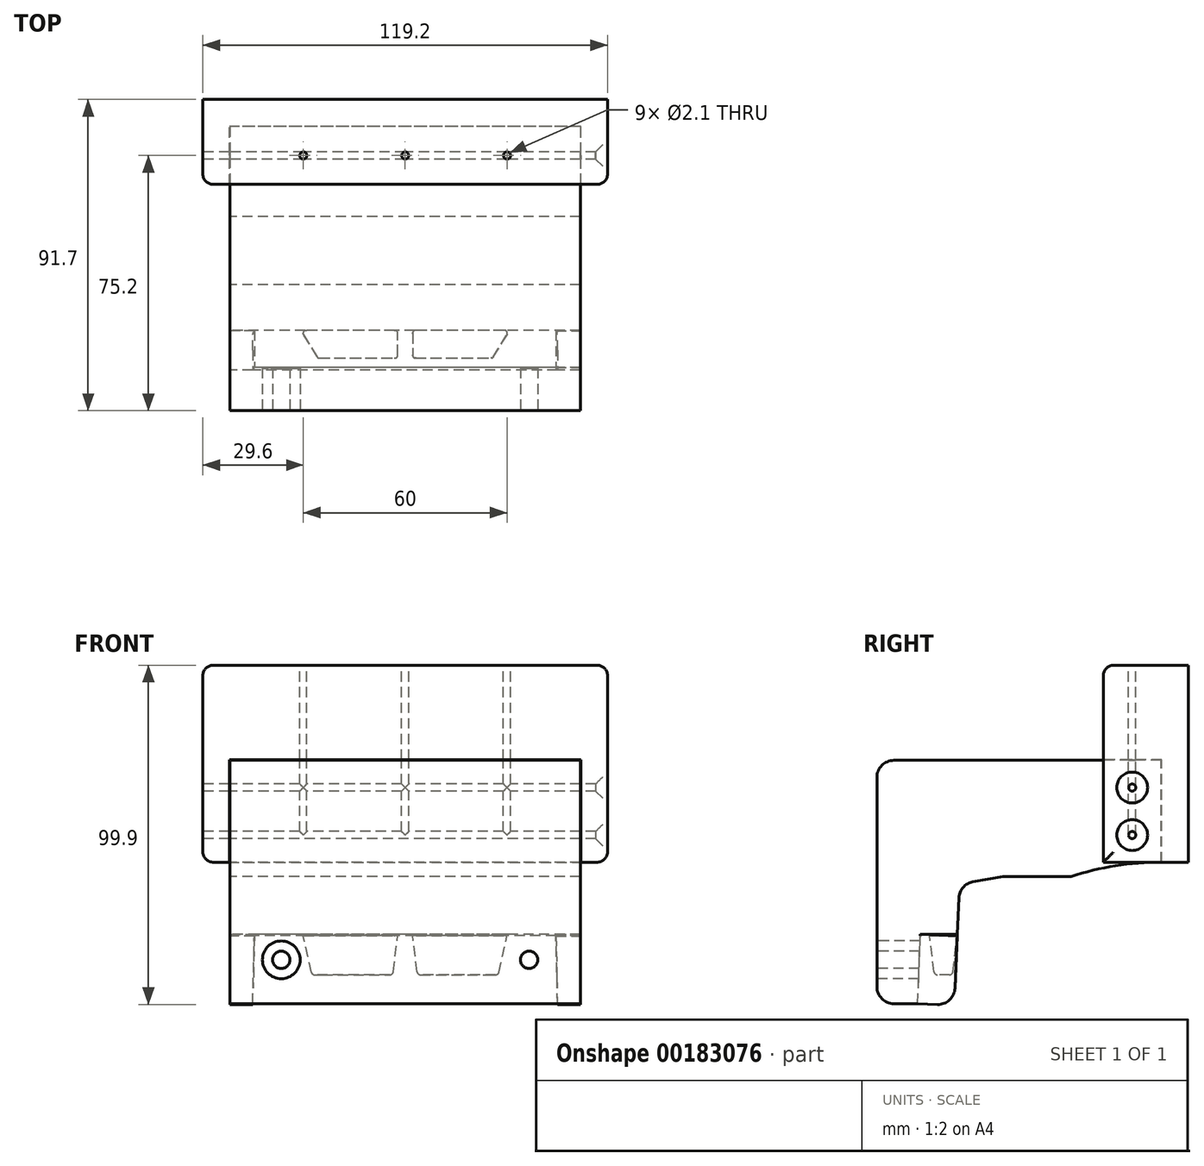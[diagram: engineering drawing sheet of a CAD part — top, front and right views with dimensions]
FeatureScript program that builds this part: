
annotation { "Feature Type Name" : "Feature", "Feature Type Description" : "" }
export const myFeature = defineFeature(function(context is Context, id is Id, definition is map)
    precondition{}
    {
        {
            assignVariable(context, id + "F0", {"name" : "T", "anyValue" : 0.2});
        }
        {
            var Q0;
            Q0=qCreatedBy(makeId("Top.planeOp"),FACE);
            var sketch = newSketch(context, id + "F1", { "sketchPlane" : qUnion([Q0])});
            skLineSegment(sketch, "E0", {"start": v(0, 12.42) * mm, "end": v(0, -41.85) * mm, "construction": true});
            skLineSegment(sketch, "E1.0", {"start": v(2.2, 0) * mm, "end": v(2.2, -8.2) * mm});
            skLineSegment(sketch, "E2", {"start": v(30.8, 0) * mm, "end": v(30.8, 0) * mm});
            skLineSegment(sketch, "E3", {"start": v(2.2, 0) * mm, "end": v(30.8, 0) * mm});
            skLineSegment(sketch, "E4", {"start": v(2.2, -8.2) * mm, "end": v(25.7, -8.2) * mm});
            skLineSegment(sketch, "E5", {"start": v(25.7, -8.2) * mm, "end": v(30.8, 0) * mm});
            skLineSegment(sketch, "E6.MirrorCS", {"start": v(-2.2, 0) * mm, "end": v(-2.2, -8.2) * mm});
            skLineSegment(sketch, "E7.MirrorCS", {"start": v(-2.2, 0) * mm, "end": v(-30.8, 0) * mm});
            skLineSegment(sketch, "E8.MirrorCS", {"start": v(-25.7, -8.2) * mm, "end": v(-30.8, 0) * mm});
            skLineSegment(sketch, "E9.MirrorCS", {"start": v(-2.2, -8.2) * mm, "end": v(-25.7, -8.2) * mm});
            skSolve(sketch);
        }
        {
            var Q0;
            Q0 = qSketchRegion(id + "F1", true);
            extrude(context, id + "F2", {"entities" : qUnion([Q0]), "oppositeDirection" : true, "depth" : 11.5 * mm, "hasDraft" : true, "draftAngle" : 7 * degree, "draftPullDirection" : true});
        }
        {
            var Q0;
            Q0=qCreatedBy(makeId("Right.planeOp"),FACE);
            var sketch = newSketch(context, id + "F3", { "sketchPlane" : qUnion([Q0])});
            skPoint(sketch, "E10.0", {"position": v(-8.2, 0) * mm});
            skLineSegment(sketch, "E11", {"start": v(-10.9, 0) * mm, "end": v(-11.7, -20) * mm});
            skLineSegment(sketch, "E12", {"start": v(-11.7, -20) * mm, "end": v(-23.7, -20) * mm});
            skLineSegment(sketch, "E13", {"start": v(-23.7, -20) * mm, "end": v(-23.7, 0) * mm});
            skLineSegment(sketch, "E14", {"start": v(-10.9, 0) * mm, "end": v(-23.7, 0) * mm});
            skSolve(sketch);
        }
        {
            var Q0;
            Q0=makeQuery(id+"F3.imprint","IMPRINT",FACE,{"disambiguationData":[TD([[makeQuery(id+"F3.imprint","IMPRINT",EDGE,{"derivedFrom":sQuery(id+"F3.wireOp",EDGE,"E11")}),-1.0]])]});
            extrude(context, id + "F4", {"entities" : qUnion([Q0]), "endBound" : BoundingType.SYMMETRIC, "depth" : (103.6 - 2 * getVariable(context, 'T')) * mm});
        }
        {
            var Q0;
            Q0=makeQuery(id+"F4.opExtrude","SWEPT_FACE",FACE,{"disambiguationData":[OSD([sQuery(id+"F3.wireOp",EDGE,"E13")])]});
            var sketch = newSketch(context, id + "F5", { "sketchPlane" : qUnion([Q0])});
            skLineSegment(sketch, "E15", {"start": v(0, 0) * mm, "end": v(0, -20) * mm, "construction": true});
            skLineSegment(sketch, "E16.0", {"start": v(36.5, 0) * mm, "end": v(36.5, -20) * mm, "construction": true});
            skLineSegment(sketch, "E17.0", {"start": v(51.6, -7.1) * mm, "end": v(-51.6, -7.1) * mm, "construction": true});
            skCircle(sketch, "E18", {"center": v(36.5, -7.1) * mm, "radius": 2.55 * mm});
            skCircle(sketch, "E19", {"center": v(36.5, -7.1) * mm, "radius": 5.55 * mm});
            skCircle(sketch, "E20.MirrorC", {"center": v(-36.5, -7.1) * mm, "radius": 2.55 * mm});
            skCircle(sketch, "E21.MirrorC", {"center": v(-36.5, -7.1) * mm, "radius": 5.55 * mm});
            skSolve(sketch);
        }
        {
            var Q0;
            Q0=makeQuery(id+"F5.imprint","IMPRINT",FACE,{"disambiguationData":[TD([[makeQuery(id+"F5.imprint","IMPRINT",EDGE,{"derivedFrom":sQuery(id+"F5.wireOp",EDGE,"E20.MirrorC")}),-1.0]])]});
            var Q1;
            Q1=makeQuery(id+"F5.imprint","IMPRINT",FACE,{"disambiguationData":[TD([[makeQuery(id+"F5.imprint","IMPRINT",EDGE,{"derivedFrom":sQuery(id+"F5.wireOp",EDGE,"E18")}),1.0]])]});
            extrude(context, id + "F6", {"entities" : qUnion([Q0, Q1]), "operationType" : NewBodyOperationType.REMOVE, "endBound" : BoundingType.THROUGH_ALL, "oppositeDirection" : true, "depth" : 25 * mm});
        }
        {
            var Q0;
            Q0=makeQuery(id+"F2.opExtrude","CAP_FACE",FACE,{"disambiguationData":[OSD([sQuery(id+"F1.wireOp",EDGE,"E6.MirrorCS"),sQuery(id+"F1.wireOp",EDGE,"E7.MirrorCS"),sQuery(id+"F1.wireOp",EDGE,"E8.MirrorCS"),sQuery(id+"F1.wireOp",EDGE,"E9.MirrorCS")])],"isStart":true});
            var Q1;
            Q1=makeQuery(id+"F2.opExtrude","CAP_FACE",FACE,{"disambiguationData":[OSD([sQuery(id+"F1.wireOp",EDGE,"E1.0"),sQuery(id+"F1.wireOp",EDGE,"E3"),sQuery(id+"F1.wireOp",EDGE,"E4"),sQuery(id+"F1.wireOp",EDGE,"E5")])],"isStart":true});
            var Q2;
            Q2=makeQuery(id+"F4.opExtrude","SWEPT_FACE",FACE,{"disambiguationData":[OSD([sQuery(id+"F3.wireOp",EDGE,"E14")])]});
            extrude(context, id + "F7", {"entities" : qUnion([Q0, Q1, Q2]), "operationType" : NewBodyOperationType.ADD, "depth" : (2 * getVariable(context, 'T')) * mm});
        }
        {
            var Q0;
            Q0=makeQuery(id+"F4.opExtrude","SWEPT_FACE",FACE,{"disambiguationData":[OSD([sQuery(id+"F3.wireOp",EDGE,"E11")])]});
            var sketch = newSketch(context, id + "F8", { "sketchPlane" : qUnion([Q0])});
            skLineSegment(sketch, "E22", {"start": v(0, -0.44) * mm, "end": v(0, -21.48) * mm, "construction": true});
            skPoint(sketch, "E22.endSnap0", {"position": v(0, -20.45) * mm});
            skLineSegment(sketch, "E23.0", {"start": v(44.4, -0.04) * mm, "end": v(44.4, -20.45) * mm});
            skLineSegment(sketch, "E24", {"start": v(51.6, -0.04) * mm, "end": v(51.6, -20.45) * mm});
            skLineSegment(sketch, "E25", {"start": v(51.6, -20.45) * mm, "end": v(44.4, -20.45) * mm});
            skPoint(sketch, "E26.0", {"position": v(51.6, -20.45) * mm});
            skLineSegment(sketch, "E27.0", {"start": v(44.4, -0.04) * mm, "end": v(51.6, -0.04) * mm});
            skPoint(sketch, "E28.orphan", {"position": v(-51.6, -0.04) * mm});
            skLineSegment(sketch, "E29.MirrorCS", {"start": v(-51.6, -20.45) * mm, "end": v(-44.4, -20.45) * mm});
            skLineSegment(sketch, "E30.MirrorCS", {"start": v(-51.6, -0.04) * mm, "end": v(-51.6, -20.45) * mm});
            skLineSegment(sketch, "E31.MirrorCS", {"start": v(-44.4, -0.04) * mm, "end": v(-44.4, -20.45) * mm});
            skLineSegment(sketch, "E32.MirrorCS", {"start": v(-44.4, -0.04) * mm, "end": v(-51.6, -0.04) * mm});
            skSolve(sketch);
        }
        {
            var Q0;
            Q0 = qSketchRegion(id + "F8", true);
            var Q1;
            {var subQ0=sQuery(id+"F8.wireOp",EDGE,"7b3c15e0-ed21-419c-adba-b3023ec59cf90.MirrorCS");Q1=makeQuery(id+"F8.imprint","IMPRINT",FACE,{"disambiguationData":[TD([[makeQuery(id+"F8.imprint","IMPRINT",EDGE,{"derivedFrom":subQ0}),-1.0]])]});}
            extrude(context, id + "F9", {"entities" : qUnion([Q0, Q1]), "operationType" : NewBodyOperationType.ADD, "depth" : (10.6 + getVariable(context, 'T')) * mm});
        }
        {
            var Q0;
            Q0=makeQuery(id+"F2.opExtrude","CAP_EDGE",EDGE,{"disambiguationData":[OSD([sQuery(id+"F1.wireOp",EDGE,"E9.MirrorCS")])],"isStart":false});
            var Q1;
            Q1=makeQuery(id+"F2.opExtrude","CAP_EDGE",EDGE,{"disambiguationData":[OSD([sQuery(id+"F1.wireOp",EDGE,"E8.MirrorCS")])],"isStart":false});
            var Q2;
            Q2=makeQuery(id+"F2.opExtrude","CAP_EDGE",EDGE,{"disambiguationData":[OSD([sQuery(id+"F1.wireOp",EDGE,"E7.MirrorCS")])],"isStart":false});
            var Q3;
            Q3=makeQuery(id+"F2.opExtrude","CAP_EDGE",EDGE,{"disambiguationData":[OSD([sQuery(id+"F1.wireOp",EDGE,"E6.MirrorCS")])],"isStart":false});
            var Q4;
            Q4=makeQuery(id+"F2.opExtrude","CAP_EDGE",EDGE,{"disambiguationData":[OSD([sQuery(id+"F1.wireOp",EDGE,"E1.0")])],"isStart":false});
            var Q5;
            Q5=makeQuery(id+"F2.opExtrude","CAP_EDGE",EDGE,{"disambiguationData":[OSD([sQuery(id+"F1.wireOp",EDGE,"E4")])],"isStart":false});
            var Q6;
            Q6=makeQuery(id+"F2.opExtrude","CAP_EDGE",EDGE,{"disambiguationData":[OSD([sQuery(id+"F1.wireOp",EDGE,"E5")])],"isStart":false});
            var Q7;
            Q7=makeQuery(id+"F2.opExtrude","CAP_EDGE",EDGE,{"disambiguationData":[OSD([sQuery(id+"F1.wireOp",EDGE,"E3")])],"isStart":false});
            var Q8;
            Q8=makeQuery(id+"F2.opExtrude","SWEPT_EDGE",EDGE,{"disambiguationData":[OSD([sQuery(id+"F1.wireOp",EDGE,"E1.0"),sQuery(id+"F1.wireOp",EDGE,"E3")])]});
            var Q9;
            Q9=makeQuery(id+"F2.opExtrude","SWEPT_EDGE",EDGE,{"disambiguationData":[OSD([sQuery(id+"F1.wireOp",EDGE,"E3"),sQuery(id+"F1.wireOp",EDGE,"E5")])]});
            var Q10;
            Q10=makeQuery(id+"F2.opExtrude","SWEPT_EDGE",EDGE,{"disambiguationData":[OSD([sQuery(id+"F1.wireOp",EDGE,"E4"),sQuery(id+"F1.wireOp",EDGE,"E5")])]});
            var Q11;
            Q11=makeQuery(id+"F2.opExtrude","SWEPT_EDGE",EDGE,{"disambiguationData":[OSD([sQuery(id+"F1.wireOp",EDGE,"E1.0"),sQuery(id+"F1.wireOp",EDGE,"E4")])]});
            var Q12;
            Q12=makeQuery(id+"F2.opExtrude","SWEPT_EDGE",EDGE,{"disambiguationData":[OSD([sQuery(id+"F1.wireOp",EDGE,"E6.MirrorCS"),sQuery(id+"F1.wireOp",EDGE,"E9.MirrorCS")])]});
            var Q13;
            Q13=makeQuery(id+"F2.opExtrude","SWEPT_EDGE",EDGE,{"disambiguationData":[OSD([sQuery(id+"F1.wireOp",EDGE,"E8.MirrorCS"),sQuery(id+"F1.wireOp",EDGE,"E9.MirrorCS")])]});
            var Q14;
            Q14=makeQuery(id+"F2.opExtrude","SWEPT_EDGE",EDGE,{"disambiguationData":[OSD([sQuery(id+"F1.wireOp",EDGE,"E7.MirrorCS"),sQuery(id+"F1.wireOp",EDGE,"E8.MirrorCS")])]});
            var Q15;
            Q15=makeQuery(id+"F2.opExtrude","SWEPT_EDGE",EDGE,{"disambiguationData":[OSD([sQuery(id+"F1.wireOp",EDGE,"E6.MirrorCS"),sQuery(id+"F1.wireOp",EDGE,"E7.MirrorCS")])]});
            fillet(context, id + "F10", {"entities" : qUnion([Q0, Q1, Q2, Q3, Q4, Q5, Q6, Q7, Q8, Q9, Q10, Q11, Q12, Q13, Q14, Q15]), "radius" : 1 * mm, "tangentPropagation" : true, "allowEdgeOverflow" : false});
        }
        {
            var Q0;
            {var subQ0=sQuery(id+"F1.wireOp",EDGE,"E7.MirrorCS");Q0=makeQuery(id+"F7.boolean.opBoolean","MERGE",EDGE,{"derivedFrom":[makeQuery(id+"F2.opExtrude","CAP_EDGE",EDGE,{"disambiguationData":[OSD([subQ0])],"isStart":true}),makeQuery(id+"F7.opExtrude","CAP_EDGE",EDGE,{"disambiguationData":[OSD([subQ0])],"isStart":true})]});}
            cPlane(context, id + "F11", {"entities" : qUnion([Q0]), "cplaneType" : CPlaneType.LINE_ANGLE, "offset" : 25 * mm, "angle" : 2.5 * degree, "width" : 150 * mm, "height" : 150 * mm});
        }
        {
            var Q0;
            Q0=qCreatedBy(makeId("Right.planeOp"),FACE);
            var sketch = newSketch(context, id + "F12", { "sketchPlane" : qUnion([Q0])});
            skPoint(sketch, "E33.0", {"position": v(-23.7, 0.4) * mm});
            skPoint(sketch, "E34.0", {"position": v(0, 0.4) * mm});
            skLineSegment(sketch, "E35", {"start": v(-23.7, 0.4) * mm, "end": v(0, 0.4) * mm});
            skLineSegment(sketch, "E36", {"start": v(-23.7, 0.4) * mm, "end": v(-23.7, 15.2) * mm});
            skLineSegment(sketch, "E37", {"start": v(-23.7, 15.2) * mm, "end": v(0.65, 15.2) * mm, "construction": true});
            skLineSegment(sketch, "E38", {"start": v(0.65, 15.2) * mm, "end": v(0, 0.4) * mm});
            skLineSegment(sketch, "E39", {"start": v(0.65, 15.2) * mm, "end": v(13.45, 17.46) * mm});
            skLineSegment(sketch, "E40", {"start": v(13.45, 17.46) * mm, "end": v(33.45, 17.46) * mm});
            skLineSegment(sketch, "E41", {"start": v(60, 51.66) * mm, "end": v(-23.7, 51.66) * mm});
            skLineSegment(sketch, "E42", {"start": v(-23.7, 51.66) * mm, "end": v(-23.7, 15.2) * mm});
            skArc(sketch, "E43", {"start": v(60, 21.66) * mm, "mid": v(46.56, 20.6) * mm, "end": v(33.45, 17.46) * mm});
            skLineSegment(sketch, "E44", {"start": v(60, 21.66) * mm, "end": v(60, 51.66) * mm});
            skSolve(sketch);
        }
        {
            var Q0;
            Q0 = qSketchRegion(id + "F12", true);
            extrude(context, id + "F13", {"entities" : qUnion([Q0]), "operationType" : NewBodyOperationType.ADD, "endBound" : BoundingType.SYMMETRIC, "depth" : 103.2 * mm});
        }
        {
            var Q0;
            {var subQ0=sQuery(id+"F3.wireOp",EDGE,"E14");Q0=makeQuery(id+"F13.boolean.opBoolean","MERGE",FACE,{"derivedFrom":[makeQuery(id+"F9.boolean.opBoolean","MERGE",FACE,{"derivedFrom":[makeQuery(id+"F7.boolean.opBoolean","MERGE",FACE,{"derivedFrom":[makeQuery(id+"F4.opExtrude","CAP_FACE",FACE,{"disambiguationData":[OSD([sQuery(id+"F3.wireOp",EDGE,"E11"),sQuery(id+"F3.wireOp",EDGE,"E12"),sQuery(id+"F3.wireOp",EDGE,"E13"),subQ0])],"isStart":true}),makeQuery(id+"F7.opExtrude","SWEPT_FACE",FACE,{"disambiguationData":[OSD([subQ0]),TDD([makeQuery(id+"F4.opExtrude","CAP_EDGE",EDGE,{"disambiguationData":[OSD([subQ0])],"isStart":true})])]})]}),makeQuery(id+"F9.opExtrude","SWEPT_FACE",FACE,{"disambiguationData":[OSD([sQuery(id+"F8.wireOp",EDGE,"E24")])]})]}),makeQuery(id+"F13.opExtrude","CAP_FACE",FACE,{"disambiguationData":[OSD([sQuery(id+"F12.wireOp",EDGE,"E35"),sQuery(id+"F12.wireOp",EDGE,"E36"),sQuery(id+"F12.wireOp",EDGE,"E38"),sQuery(id+"F12.wireOp",EDGE,"E39"),sQuery(id+"F12.wireOp",EDGE,"E40"),sQuery(id+"F12.wireOp",EDGE,"E41"),sQuery(id+"F12.wireOp",EDGE,"E42"),sQuery(id+"F12.wireOp",EDGE,"E43"),sQuery(id+"F12.wireOp",EDGE,"E44")])],"isStart":true})]});}
            var sketch = newSketch(context, id + "F14", { "sketchPlane" : qUnion([Q0])});
            skLineSegment(sketch, "E45", {"start": v(0.27, -4.52) * mm, "end": v(12.26, -4.04) * mm});
            skLineSegment(sketch, "E46", {"start": v(12.26, -4.04) * mm, "end": v(11.98, 2.96) * mm});
            skLineSegment(sketch, "E47", {"start": v(11.98, 2.96) * mm, "end": v(-0.11, 2.96) * mm});
            skLineSegment(sketch, "E48", {"start": v(0.27, -4.52) * mm, "end": v(0.1, -0.03) * mm});
            skLineSegment(sketch, "E49", {"start": v(0.1, -0.03) * mm, "end": v(-0.11, 2.96) * mm});
            skSolve(sketch);
        }
        {
            var Q0;
            Q0 = qSketchRegion(id + "F14", true);
            var Q1;
            Q1=makeQuery(id+"F9.opExtrude","SWEPT_FACE",FACE,{"disambiguationData":[OSD([sQuery(id+"F8.wireOp",EDGE,"E23.0")])]});
            extrude(context, id + "F15", {"entities" : qUnion([Q0]), "operationType" : NewBodyOperationType.ADD, "oppositeDirection" : true, "endBoundEntityFace" : qUnion([Q1]), "depth" : 7.2 * mm});
        }
        {
            var Q0;
            Q0=makeQuery(id+"F4.opExtrude","SWEPT_EDGE",EDGE,{"disambiguationData":[OSD([sQuery(id+"F3.wireOp",EDGE,"E12"),sQuery(id+"F3.wireOp",EDGE,"E13")])]});
            var Q1;
            Q1=makeQuery(id+"F13.opExtrude","SWEPT_EDGE",EDGE,{"disambiguationData":[OSD([sQuery(id+"F12.wireOp",EDGE,"E41"),sQuery(id+"F12.wireOp",EDGE,"E42")])]});
            var Q2;
            Q2=makeQuery(id+"F13.opExtrude","SWEPT_EDGE",EDGE,{"disambiguationData":[OSD([sQuery(id+"F12.wireOp",EDGE,"E38"),sQuery(id+"F12.wireOp",EDGE,"E39")])]});
            var Q3;
            Q3=makeQuery(id+"F9.opExtrude","CAP_EDGE",EDGE,{"disambiguationData":[OSD([sQuery(id+"F8.wireOp",EDGE,"E25")])],"isStart":false});
            var Q4;
            Q4=makeQuery(id+"F9.opExtrude","CAP_EDGE",EDGE,{"disambiguationData":[OSD([sQuery(id+"F8.wireOp",EDGE,"E29.MirrorCS")])],"isStart":false});
            fillet(context, id + "F16", {"entities" : qUnion([Q0, Q1, Q2, Q3, Q4]), "radius" : 5 * mm, "tangentPropagation" : true, "allowEdgeOverflow" : false});
        }
        {
            var Q0;
            Q0=makeQuery(id+"F4.opExtrude","SWEPT_FACE",FACE,{"disambiguationData":[OSD([sQuery(id+"F3.wireOp",EDGE,"E11")])]});
            var sketch = newSketch(context, id + "F17", { "sketchPlane" : qUnion([Q0])});
            skLineSegment(sketch, "E50.0", {"start": v(44.4, -0.44) * mm, "end": v(44.4, -20.45) * mm});
            skLineSegment(sketch, "E51.0", {"start": v(44.4, -0.04) * mm, "end": v(44.4, -0.44) * mm});
            skLineSegment(sketch, "E52.0", {"start": v(-44.4, -0.44) * mm, "end": v(-44.4, -20.45) * mm});
            skLineSegment(sketch, "E53.0", {"start": v(-44.4, -0.44) * mm, "end": v(-44.4, -0.04) * mm});
            skLineSegment(sketch, "E54", {"start": v(0, 6.93) * mm, "end": v(0, -38.14) * mm, "construction": true});
            skLineSegment(sketch, "E55", {"start": v(-44.9, -20.45) * mm, "end": v(-44.4, -0.04) * mm});
            skLineSegment(sketch, "E56", {"start": v(-44.9, -20.45) * mm, "end": v(-44.4, -20.45) * mm});
            skLineSegment(sketch, "E57.MirrorCS", {"start": v(44.9, -20.45) * mm, "end": v(44.4, -20.45) * mm});
            skLineSegment(sketch, "E58.MirrorCS", {"start": v(44.9, -20.45) * mm, "end": v(44.4, -0.04) * mm});
            skSolve(sketch);
        }
        {
            var Q0;
            Q0 = qSketchRegion(id + "F17", true);
            extrude(context, id + "F18", {"entities" : qUnion([Q0]), "operationType" : NewBodyOperationType.REMOVE, "endBound" : BoundingType.THROUGH_ALL, "depth" : 25 * mm});
        }
        {
            var Q0;
            Q0=makeQuery(id+"F13.opExtrude","SWEPT_FACE",FACE,{"disambiguationData":[OSD([sQuery(id+"F12.wireOp",EDGE,"E44")])]});
            cPlane(context, id + "F19", {"entities" : qUnion([Q0]), "cplaneType" : CPlaneType.OFFSET, "offset" : 8 * mm, "width" : 150 * mm, "height" : 150 * mm});
        }
        {
            var Q0;
            Q0=qCreatedBy(id+"F19.planeOp",FACE);
            var sketch = newSketch(context, id + "F20", { "sketchPlane" : qUnion([Q0])});
            skLineSegment(sketch, "E59.0", {"start": v(-59.6, 79.66) * mm, "end": v(59.6, 79.66) * mm});
            skLineSegment(sketch, "E60.0", {"start": v(59.6, 21.66) * mm, "end": v(59.6, 79.66) * mm});
            skLineSegment(sketch, "E61.0", {"start": v(-59.6, 21.66) * mm, "end": v(-59.6, 79.66) * mm});
            skLineSegment(sketch, "E62.0", {"start": v(-51.6, 21.66) * mm, "end": v(51.6, 21.66) * mm});
            skLineSegment(sketch, "E63", {"start": v(59.6, 21.66) * mm, "end": v(51.6, 21.66) * mm});
            skLineSegment(sketch, "E64", {"start": v(-59.6, 21.66) * mm, "end": v(-51.6, 21.66) * mm});
            skSolve(sketch);
        }
        {
            var Q0;
            Q0 = qSketchRegion(id + "F20", true);
            extrude(context, id + "F21", {"entities" : qUnion([Q0]), "oppositeDirection" : true, "depth" : 25 * mm});
        }
        {
            var Q0;
            Q0=makeQuery(id+"F2.opExtrude","SWEPT_BODY",BODY,{"disambiguationData":[OSD([sQuery(id+"F1.wireOp",EDGE,"E1.0"),sQuery(id+"F1.wireOp",EDGE,"E3"),sQuery(id+"F1.wireOp",EDGE,"E4"),sQuery(id+"F1.wireOp",EDGE,"E5")])]});
            var Q1;
            Q1=makeQuery(id+"F21.opExtrude","SWEPT_BODY",BODY,{"disambiguationData":[OSD([sQuery(id+"F20.wireOp",EDGE,"E59.0"),sQuery(id+"F20.wireOp",EDGE,"E60.0"),sQuery(id+"F20.wireOp",EDGE,"E61.0"),sQuery(id+"F20.wireOp",EDGE,"E62.0"),sQuery(id+"F20.wireOp",EDGE,"E63"),sQuery(id+"F20.wireOp",EDGE,"E64")])]});
            booleanBodies(context, id + "F22", {"operationType" : BooleanOperationType.SUBTRACTION, "tools" : qUnion([Q0]), "targets" : qUnion([Q1]), "offset" : true, "offsetAll" : true, "offsetDistance" : .2 * mm, "keepTools" : true});
        }
        {
            var Q0;
            Q0=makeQuery(id+"F21.opExtrude","SWEPT_FACE",FACE,{"disambiguationData":[OSD([sQuery(id+"F20.wireOp",EDGE,"E60.0")])]});
            var sketch = newSketch(context, id + "F23", { "sketchPlane" : qUnion([Q0])});
            skPoint(sketch, "E65.0", {"position": v(-60, 21.66) * mm});
            skLineSegment(sketch, "E66", {"start": v(-60, 21.66) * mm, "end": v(-43, 79.66) * mm, "construction": true});
            skCircle(sketch, "E67", {"center": v(-51.5, 29.66) * mm, "radius": 1.05 * mm});
            skPoint(sketch, "E68", {"position": v(-51.5, 50.66) * mm});
            skLineSegment(sketch, "E69", {"start": v(-51.5, 79.66) * mm, "end": v(-51.5, 21.66) * mm, "construction": true});
            skCircle(sketch, "E70", {"center": v(-51.5, 43.66) * mm, "radius": 1.05 * mm});
            skSolve(sketch);
        }
        {
            var Q0;
            Q0 = qSketchRegion(id + "F23", true);
            extrude(context, id + "F24", {"entities" : qUnion([Q0]), "operationType" : NewBodyOperationType.REMOVE, "endBound" : BoundingType.THROUGH_ALL, "oppositeDirection" : true, "depth" : 25 * mm});
        }
        {
            var Q0;
            Q0=makeQuery(id+"F21.opExtrude","SWEPT_FACE",FACE,{"disambiguationData":[OSD([sQuery(id+"F20.wireOp",EDGE,"E59.0")])]});
            var sketch = newSketch(context, id + "F25", { "sketchPlane" : qUnion([Q0])});
            skLineSegment(sketch, "E71.0", {"start": v(51.6, 60) * mm, "end": v(-51.6, 60) * mm, "construction": true});
            skLineSegment(sketch, "E72.0", {"start": v(59.6, 43) * mm, "end": v(-59.6, 43) * mm, "construction": true});
            skLineSegment(sketch, "E73", {"start": v(-51.6, 60) * mm, "end": v(-59.6, 60) * mm, "construction": true});
            skLineSegment(sketch, "E74", {"start": v(-59.6, 60) * mm, "end": v(59.6, 43) * mm, "construction": true});
            skLineSegment(sketch, "E75", {"start": v(59.6, 51.5) * mm, "end": v(-59.6, 51.5) * mm, "construction": true});
            skPoint(sketch, "E75.startSnap0", {"position": v(0, 51.5) * mm});
            skCircle(sketch, "E76", {"center": v(0, 51.5) * mm, "radius": 1.05 * mm});
            skCircle(sketch, "E77.0.1.0", {"center": v(-30, 51.5) * mm, "radius": 1.05 * mm});
            skCircle(sketch, "E77.1.0.0", {"center": v(30, 51.5) * mm, "radius": 1.05 * mm});
            skLineSegment(sketch, "E77.direction1", {"start": v(0, 51.5) * mm, "end": v(30, 51.5) * mm, "construction": true});
            skLineSegment(sketch, "E77.direction2", {"start": v(0, 51.5) * mm, "end": v(-30, 51.5) * mm, "construction": true});
            skSolve(sketch);
        }
        {
            var Q0;
            Q0 = qSketchRegion(id + "F25", true);
            extrude(context, id + "F26", {"entities" : qUnion([Q0]), "operationType" : NewBodyOperationType.REMOVE, "oppositeDirection" : true, "depth" : 50 * mm});
        }
        {
            var Q0;
            Q0=makeQuery(id+"F24.boolean.opBoolean","COPY",EDGE,{"derivedFrom":makeQuery(id+"F24.opExtrude","CAP_EDGE",EDGE,{"disambiguationData":[OSD([sQuery(id+"F23.wireOp",EDGE,"E67")])],"isStart":true})});
            var Q1;
            Q1=makeQuery(id+"F24.boolean.opBoolean","COPY",EDGE,{"derivedFrom":makeQuery(id+"F24.opExtrude","CAP_EDGE",EDGE,{"disambiguationData":[OSD([sQuery(id+"F23.wireOp",EDGE,"E70")])],"isStart":true})});
            var Q2;
            Q2=makeQuery(id+"F26.boolean.opBoolean","COPY",EDGE,{"derivedFrom":makeQuery(id+"F26.opExtrude","CAP_EDGE",EDGE,{"disambiguationData":[OSD([sQuery(id+"F25.wireOp",EDGE,"E77.0.1.0")])],"isStart":true})});
            var Q3;
            Q3=makeQuery(id+"F26.boolean.opBoolean","COPY",EDGE,{"derivedFrom":makeQuery(id+"F26.opExtrude","CAP_EDGE",EDGE,{"disambiguationData":[OSD([sQuery(id+"F25.wireOp",EDGE,"E76")])],"isStart":true})});
            var Q4;
            Q4=makeQuery(id+"F26.boolean.opBoolean","COPY",EDGE,{"derivedFrom":makeQuery(id+"F26.opExtrude","CAP_EDGE",EDGE,{"disambiguationData":[OSD([sQuery(id+"F25.wireOp",EDGE,"E77.1.0.0")])],"isStart":true})});
            var Q5;
            Q5=makeQuery(id+"F24.boolean.opBoolean","INTERSECT",EDGE,{"derivedFrom":[makeQuery(id+"F21.opExtrude","SWEPT_FACE",FACE,{"disambiguationData":[OSD([sQuery(id+"F20.wireOp",EDGE,"E61.0")])]}),makeQuery(id+"F24.opExtrude","SWEPT_FACE",FACE,{"disambiguationData":[OSD([sQuery(id+"F23.wireOp",EDGE,"E70")])]})]});
            var Q6;
            Q6=makeQuery(id+"F24.boolean.opBoolean","INTERSECT",EDGE,{"derivedFrom":[makeQuery(id+"F21.opExtrude","SWEPT_FACE",FACE,{"disambiguationData":[OSD([sQuery(id+"F20.wireOp",EDGE,"E61.0")])]}),makeQuery(id+"F24.opExtrude","SWEPT_FACE",FACE,{"disambiguationData":[OSD([sQuery(id+"F23.wireOp",EDGE,"E67")])]})]});
            chamfer(context, id + "F27", {"entities" : qUnion([Q0, Q1, Q2, Q3, Q4, Q5, Q6]), "width" : 3.5 * mm, "tangentPropagation" : true});
        }
        {
            var Q0;
            Q0=makeQuery(id+"F21.opExtrude","SWEPT_EDGE",EDGE,{"disambiguationData":[OSD([sQuery(id+"F20.wireOp",EDGE,"E59.0"),sQuery(id+"F20.wireOp",EDGE,"E60.0")])]});
            var Q1;
            Q1=makeQuery(id+"F21.opExtrude","SWEPT_EDGE",EDGE,{"disambiguationData":[OSD([sQuery(id+"F20.wireOp",EDGE,"E59.0"),sQuery(id+"F20.wireOp",EDGE,"E61.0")])]});
            var Q2;
            Q2=makeQuery(id+"F21.opExtrude","CAP_EDGE",EDGE,{"disambiguationData":[OSD([sQuery(id+"F20.wireOp",EDGE,"E59.0")])],"isStart":false});
            var Q3;
            Q3=makeQuery(id+"F21.opExtrude","CAP_EDGE",EDGE,{"disambiguationData":[OSD([sQuery(id+"F20.wireOp",EDGE,"E60.0")])],"isStart":false});
            var Q4;
            Q4=makeQuery(id+"F21.opExtrude","CAP_EDGE",EDGE,{"disambiguationData":[OSD([sQuery(id+"F20.wireOp",EDGE,"E61.0")])],"isStart":false});
            var Q5;
            Q5=makeQuery(id+"F21.opExtrude","SWEPT_EDGE",EDGE,{"disambiguationData":[OSD([sQuery(id+"F20.wireOp",EDGE,"E61.0"),sQuery(id+"F20.wireOp",EDGE,"E64")])]});
            var Q6;
            Q6=makeQuery(id+"F21.opExtrude","SWEPT_EDGE",EDGE,{"disambiguationData":[OSD([sQuery(id+"F20.wireOp",EDGE,"E60.0"),sQuery(id+"F20.wireOp",EDGE,"E63")])]});
            fillet(context, id + "F28", {"entities" : qUnion([Q0, Q1, Q2, Q3, Q4, Q5, Q6]), "radius" : 3 * mm, "tangentPropagation" : true, "allowEdgeOverflow" : false});
        }
    });
